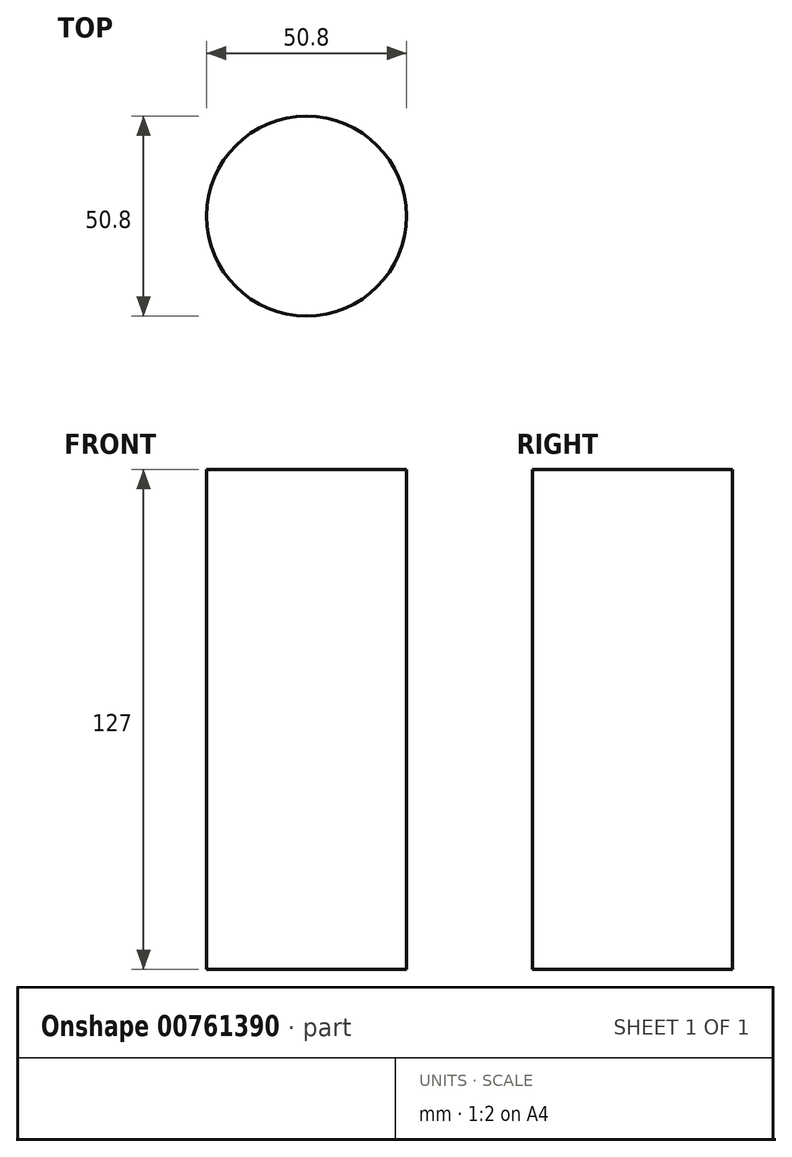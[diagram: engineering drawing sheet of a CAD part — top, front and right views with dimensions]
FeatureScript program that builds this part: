
annotation { "Feature Type Name" : "Feature", "Feature Type Description" : "" }
export const myFeature = defineFeature(function(context is Context, id is Id, definition is map)
    precondition{}
    {
        {
            var Q0;
            Q0=qCreatedBy(makeId("Top.planeOp"),FACE);
            var sketch = newSketch(context, id + "F0", { "sketchPlane" : qUnion([Q0])});
            skCircle(sketch, "E0", {"center": v(0, 0) * mm, "radius": 25.4 * mm});
            skSolve(sketch);
        }
        {
            var Q0;
            Q0 = qSketchRegion(id + "F0", true);
            extrude(context, id + "F1", {"entities" : qUnion([Q0]), "depth" : 127 * mm, "offsetDistance" : 25.4 * mm});
        }
    });
